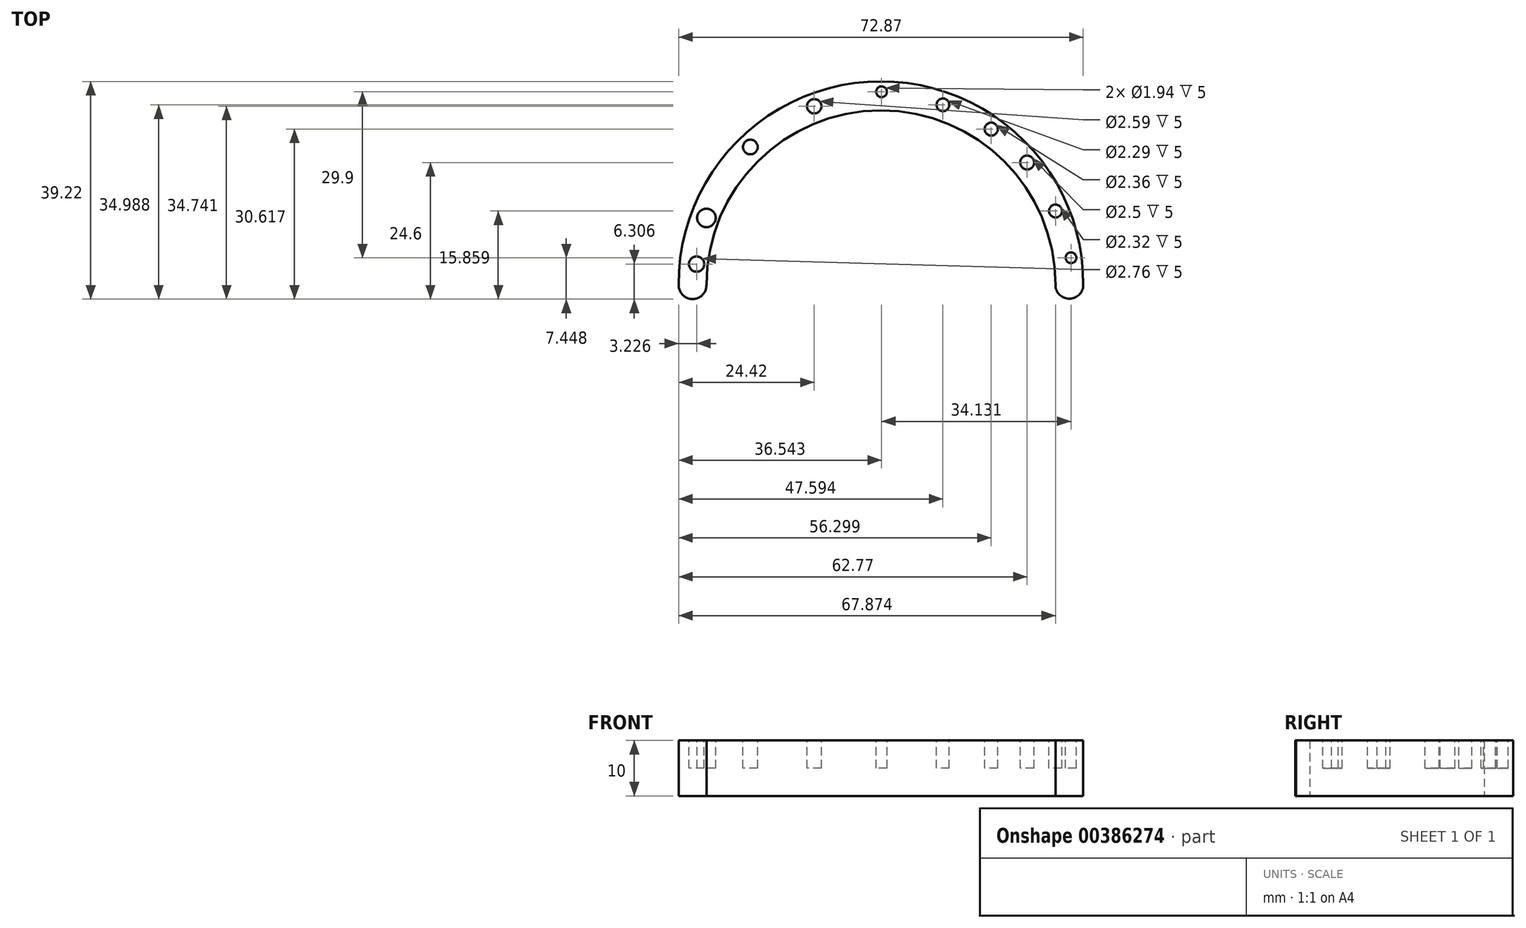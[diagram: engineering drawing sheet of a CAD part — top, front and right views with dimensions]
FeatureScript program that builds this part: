
annotation { "Feature Type Name" : "Feature", "Feature Type Description" : "" }
export const myFeature = defineFeature(function(context is Context, id is Id, definition is map)
    precondition{}
    {
        {
            var Q0;
            Q0=qCreatedBy(makeId("Top.planeOp"),FACE);
            var sketch = newSketch(context, id + "F0", { "sketchPlane" : qUnion([Q0])});
            skArc(sketch, "E0", {"start": v(62.87, 0) * mm, "mid": v(31.44, 31.44) * mm, "end": v(0, 0) * mm});
            skArc(sketch, "E1", {"start": v(62.87, 0) * mm, "mid": v(65.37, -2.5) * mm, "end": v(67.87, 0) * mm});
            skArc(sketch, "E2", {"start": v(-5, 0) * mm, "mid": v(-2.5, -2.56) * mm, "end": v(0, 0) * mm});
            skArc(sketch, "E3", {"start": v(67.87, 0) * mm, "mid": v(31.44, 36.66) * mm, "end": v(-5, 0) * mm});
            skSolve(sketch);
        }
        {
            var Q0;
            Q0=makeQuery(id+"F0.imprint","IMPRINT",FACE,{"disambiguationData":[TD([[makeQuery(id+"F0.imprint","IMPRINT",EDGE,{"derivedFrom":sQuery(id+"F0.wireOp",EDGE,"E0")}),-1.0]])]});
            extrude(context, id + "F1", {"entities" : qUnion([Q0]), "depth" : 10 * mm});
        }
        {
            var Q0;
            Q0=makeQuery(id+"F1.opExtrude","CAP_FACE",FACE,{"disambiguationData":[OSD([sQuery(id+"F0.wireOp",EDGE,"E0"),sQuery(id+"F0.wireOp",EDGE,"E1"),sQuery(id+"F0.wireOp",EDGE,"E2"),sQuery(id+"F0.wireOp",EDGE,"E3")])],"isStart":false});
            var sketch = newSketch(context, id + "F2", { "sketchPlane" : qUnion([Q0])});
            skCircle(sketch, "E4", {"center": v(0, 12.07) * mm, "radius": 1.67 * mm});
            skCircle(sketch, "E5", {"center": v(7.92, 24.84) * mm, "radius": 1.32 * mm});
            skCircle(sketch, "E6", {"center": v(19.42, 32.18) * mm, "radius": 1.3 * mm});
            skCircle(sketch, "E7", {"center": v(31.54, 34.79) * mm, "radius": 0.97 * mm});
            skCircle(sketch, "E8", {"center": v(42.6, 32.43) * mm, "radius": 1.14 * mm});
            skCircle(sketch, "E9", {"center": v(51.3, 28.06) * mm, "radius": 1.18 * mm});
            skCircle(sketch, "E10", {"center": v(57.77, 22.04) * mm, "radius": 1.25 * mm});
            skCircle(sketch, "E11", {"center": v(62.87, 13.3) * mm, "radius": 1.16 * mm});
            skCircle(sketch, "E12", {"center": v(65.67, 4.89) * mm, "radius": 0.97 * mm});
            skCircle(sketch, "E13", {"center": v(-1.77, 3.75) * mm, "radius": 1.38 * mm});
            skSolve(sketch);
        }
        {
            var Q0;
            Q0 = qSketchRegion(id + "F2", true);
            extrude(context, id + "F3", {"entities" : qUnion([Q0]), "operationType" : NewBodyOperationType.REMOVE, "oppositeDirection" : true, "depth" : 5 * mm});
        }
    });
